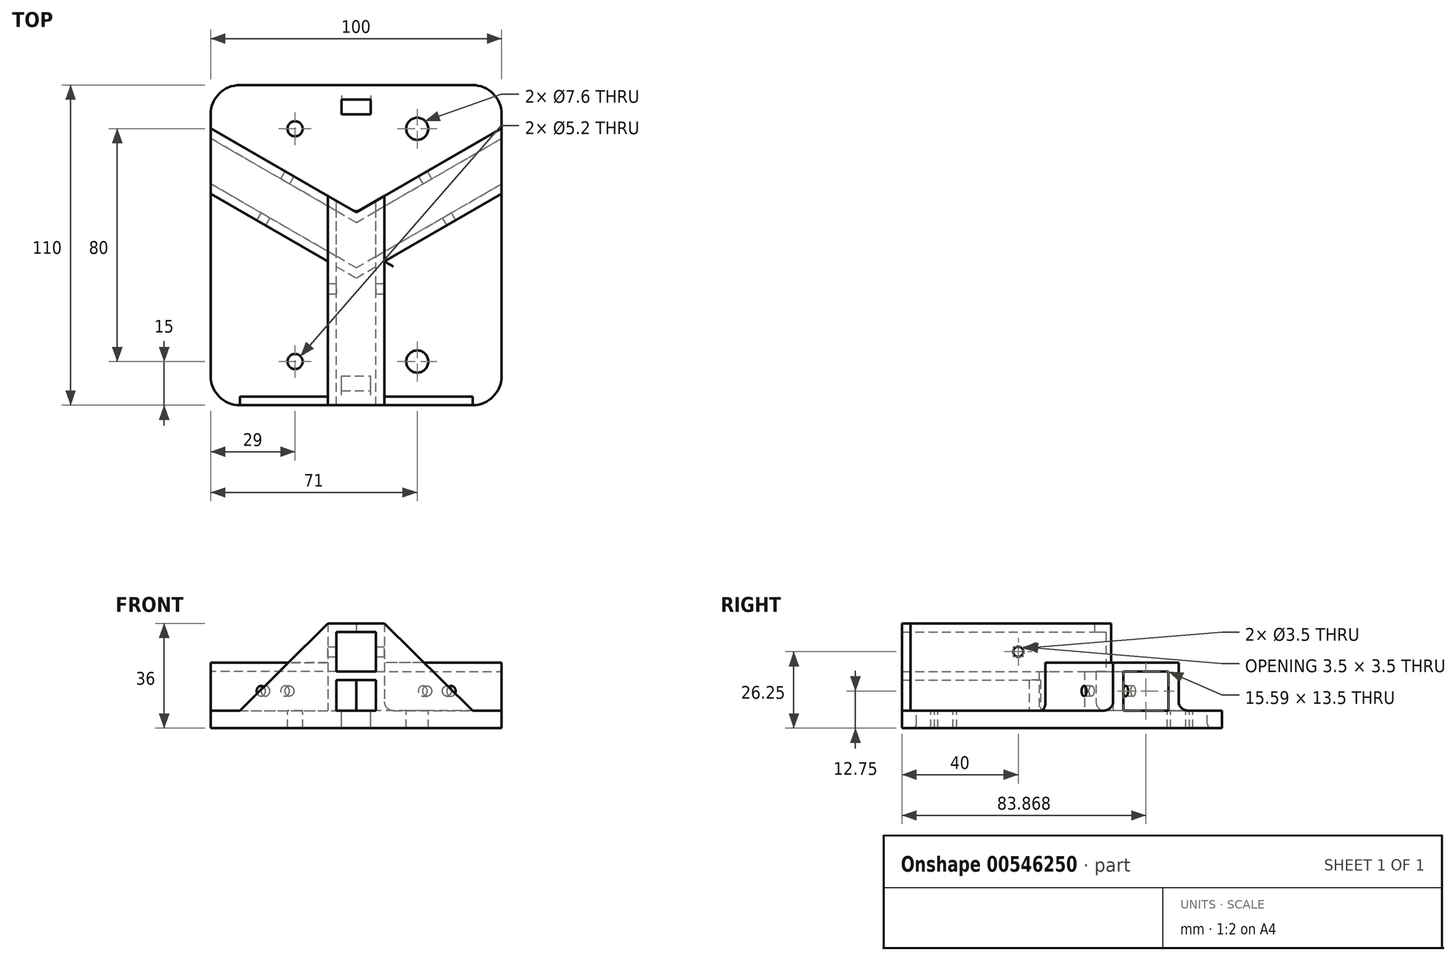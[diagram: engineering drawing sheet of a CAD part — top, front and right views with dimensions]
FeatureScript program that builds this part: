
annotation { "Feature Type Name" : "Feature", "Feature Type Description" : "" }
export const myFeature = defineFeature(function(context is Context, id is Id, definition is map)
    precondition{}
    {
        {
            var Q0;
            Q0=qCreatedBy(makeId("Top.planeOp"),FACE);
            var sketch = newSketch(context, id + "F0", { "sketchPlane" : qUnion([Q0])});
            skLineSegment(sketch, "E0.bottom", {"start": v(-50, 55) * mm, "end": v(50, 55) * mm});
            skLineSegment(sketch, "E0.top", {"start": v(-50, -55) * mm, "end": v(50, -55) * mm});
            skLineSegment(sketch, "E0.left", {"start": v(-50, 55) * mm, "end": v(-50, -55) * mm});
            skLineSegment(sketch, "E0.right", {"start": v(50, 55) * mm, "end": v(50, -55) * mm});
            skPoint(sketch, "E1", {"position": v(0, 55) * mm});
            skPoint(sketch, "E2", {"position": v(50, 0) * mm});
            skSolve(sketch);
        }
        {
            var Q0;
            Q0=qSketchRegion(id+"F0",true);
            extrude(context, id + "F1", {"entities" : qUnion([Q0]), "depth" : 6 * mm, "offsetDistance" : 25 * mm});
        }
        {
            var Q0;
            Q0=makeQuery(id+"F1.opExtrude","CAP_FACE",FACE,{"disambiguationData":[OSD([sQuery(id+"F0.wireOp",EDGE,"E0.bottom"),sQuery(id+"F0.wireOp",EDGE,"E0.top"),sQuery(id+"F0.wireOp",EDGE,"E0.left"),sQuery(id+"F0.wireOp",EDGE,"E0.right")])],"isStart":false});
            var sketch = newSketch(context, id + "F2", { "sketchPlane" : qUnion([Q0])});
            skLineSegment(sketch, "E3.bottom", {"start": v(-5, 50) * mm, "end": v(5, 50) * mm});
            skLineSegment(sketch, "E3.top", {"start": v(-5, 45) * mm, "end": v(5, 45) * mm});
            skLineSegment(sketch, "E3.left", {"start": v(-5, 50) * mm, "end": v(-5, 45) * mm});
            skLineSegment(sketch, "E3.right", {"start": v(5, 50) * mm, "end": v(5, 45) * mm});
            skPoint(sketch, "E4", {"position": v(0, 50) * mm});
            skLineSegment(sketch, "E5.MirrorCS", {"start": v(5, -50) * mm, "end": v(5, -45) * mm});
            skPoint(sketch, "E6.MirrorP", {"position": v(0, -50) * mm});
            skLineSegment(sketch, "E7.MirrorCS", {"start": v(-5, -50) * mm, "end": v(5, -50) * mm});
            skLineSegment(sketch, "E8.MirrorCS", {"start": v(-5, -50) * mm, "end": v(-5, -45) * mm});
            skLineSegment(sketch, "E9.MirrorCS", {"start": v(-5, -45) * mm, "end": v(5, -45) * mm});
            skSolve(sketch);
        }
        {
            var Q0;
            Q0=qSketchRegion(id+"F2",true);
            extrude(context, id + "F3", {"entities" : qUnion([Q0]), "operationType" : NewBodyOperationType.REMOVE, "endBound" : BoundingType.THROUGH_ALL, "oppositeDirection" : true, "depth" : 25 * mm, "offsetDistance" : 25 * mm});
        }
        {
            var Q0;
            Q0=makeQuery(id+"F1.opExtrude","CAP_FACE",FACE,{"disambiguationData":[OSD([sQuery(id+"F0.wireOp",EDGE,"E0.bottom"),sQuery(id+"F0.wireOp",EDGE,"E0.top"),sQuery(id+"F0.wireOp",EDGE,"E0.left"),sQuery(id+"F0.wireOp",EDGE,"E0.right")])],"isStart":false});
            var sketch = newSketch(context, id + "F4", { "sketchPlane" : qUnion([Q0])});
            skLineSegment(sketch, "E10", {"start": v(0, 0) * mm, "end": v(-68.17, 39.36) * mm, "construction": true});
            skLineSegment(sketch, "E11.MirrorCS", {"start": v(0, 0) * mm, "end": v(68.17, 39.36) * mm, "construction": true});
            skPoint(sketch, "E12.orphan", {"position": v(-19.52, -33.09) * mm});
            skPoint(sketch, "E13.right.end.orphan", {"position": v(19.52, -33.09) * mm});
            skLineSegment(sketch, "E14", {"start": v(0, -7.8) * mm, "end": v(50, 21.07) * mm});
            skLineSegment(sketch, "E15", {"start": v(50, 21.07) * mm, "end": v(50, 17.6) * mm});
            skLineSegment(sketch, "E16", {"start": v(50, 17.6) * mm, "end": v(9.75, -5.63) * mm});
            skLineSegment(sketch, "E17", {"start": v(0, 7.8) * mm, "end": v(50, 36.66) * mm});
            skLineSegment(sketch, "E18", {"start": v(50, 36.66) * mm, "end": v(50, 40.13) * mm});
            skLineSegment(sketch, "E19", {"start": v(50, 40.13) * mm, "end": v(0, 11.26) * mm});
            skLineSegment(sketch, "E20.MirrorCS", {"start": v(-50, 40.13) * mm, "end": v(0, 11.26) * mm});
            skLineSegment(sketch, "E21.MirrorCS", {"start": v(-50, 36.66) * mm, "end": v(-50, 40.13) * mm});
            skLineSegment(sketch, "E22.MirrorCS", {"start": v(0, 7.8) * mm, "end": v(-50, 36.66) * mm});
            skLineSegment(sketch, "E23.MirrorCS", {"start": v(0, -7.8) * mm, "end": v(-50, 21.07) * mm});
            skLineSegment(sketch, "E24.MirrorCS", {"start": v(-50, 21.07) * mm, "end": v(-50, 17.6) * mm});
            skLineSegment(sketch, "E25.MirrorCS", {"start": v(-50, 17.6) * mm, "end": v(-9.75, -5.63) * mm});
            skLineSegment(sketch, "E26", {"start": v(-6.75, -55) * mm, "end": v(-6.75, -7.36) * mm});
            skLineSegment(sketch, "E27", {"start": v(-9.75, -5.63) * mm, "end": v(-9.75, -55) * mm});
            skLineSegment(sketch, "E28", {"start": v(-9.75, -55) * mm, "end": v(-6.75, -55) * mm});
            skLineSegment(sketch, "E29.MirrorCS", {"start": v(9.75, -5.63) * mm, "end": v(9.75, -55) * mm});
            skLineSegment(sketch, "E30.MirrorCS", {"start": v(9.75, -55) * mm, "end": v(6.75, -55) * mm});
            skLineSegment(sketch, "E31.MirrorCS", {"start": v(6.75, -55) * mm, "end": v(6.75, -7.36) * mm});
            skLineSegment(sketch, "E32.trimOffspring", {"start": v(-6.75, -7.36) * mm, "end": v(0, -11.26) * mm});
            skLineSegment(sketch, "E33.trimOffspring", {"start": v(6.75, -7.36) * mm, "end": v(0, -11.26) * mm});
            skSolve(sketch);
        }
        {
            var Q0;
            {var subQ2=sQuery(id+"F0.wireOp",EDGE,"E0.right");var subQ3=makeQuery(id+"F1.opExtrude","SWEPT_FACE",FACE,{"disambiguationData":[OSD([subQ2])]});var subQ4=sQuery(id+"F0.wireOp",EDGE,"E0.top");var subQ5=makeQuery(id+"F1.opExtrude","SWEPT_FACE",FACE,{"disambiguationData":[OSD([subQ4])]});var subQ6=sQuery(id+"F0.wireOp",EDGE,"E0.left");Q0=makeQuery(id+"FRnbRCNZirlfwO5_1.boolean.opBoolean","SPLIT",FACE,{"disambiguationData":[TD([subQ3])],"derivedFrom":makeQuery(id+"F2k25GQCj0JztAD_1.boolean.opBoolean","SPLIT",FACE,{"disambiguationData":[TD([subQ5])],"derivedFrom":makeQuery(id+"F1.opExtrude","CAP_FACE",FACE,{"disambiguationData":[OSD([sQuery(id+"F0.wireOp",EDGE,"E0.bottom"),subQ4,subQ6,subQ2])],"isStart":false})})});}
            var sketch = newSketch(context, id + "F5", { "sketchPlane" : qUnion([Q0])});
            skCircle(sketch, "E34", {"center": v(21, -40) * mm, "radius": 3.8 * mm});
            skCircle(sketch, "E35", {"center": v(21, 40) * mm, "radius": 3.8 * mm});
            skCircle(sketch, "E36", {"center": v(-21, 40) * mm, "radius": 2.6 * mm});
            skCircle(sketch, "E37", {"center": v(-21, -40) * mm, "radius": 2.6 * mm});
            skSolve(sketch);
        }
        {
            var Q0;
            Q0=qSketchRegion(id+"F5",true);
            extrude(context, id + "F6", {"entities" : qUnion([Q0]), "operationType" : NewBodyOperationType.REMOVE, "endBound" : BoundingType.THROUGH_ALL, "oppositeDirection" : true, "depth" : 25 * mm, "offsetDistance" : 25 * mm});
        }
        {
            var Q0;
            Q0=qSketchRegion(id+"F4",true);
            extrude(context, id + "F7", {"entities" : qUnion([Q0]), "operationType" : NewBodyOperationType.ADD, "depth" : 13.5 * mm, "offsetDistance" : 25 * mm});
        }
        {
            var Q0;
            {var subQ0=sQuery(id+"F0.wireOp",EDGE,"E0.top");Q0=makeQuery(id+"F7.boolean.opBoolean","SPLIT",FACE,{"disambiguationData":[TD([makeQuery(id+"F3.boolean.opBoolean","COPY",FACE,{"derivedFrom":makeQuery(id+"F3.opExtrude","SWEPT_FACE",FACE,{"disambiguationData":[OSD([sQuery(id+"F2.wireOp",EDGE,"E5.MirrorCS")])]})})])],"derivedFrom":makeQuery(id+"F1.opExtrude","CAP_FACE",FACE,{"disambiguationData":[OSD([sQuery(id+"F0.wireOp",EDGE,"E0.bottom"),subQ0,sQuery(id+"F0.wireOp",EDGE,"E0.left"),sQuery(id+"F0.wireOp",EDGE,"E0.right")])],"isStart":false})});}
            cPlane(context, id + "F8", {"entities" : qUnion([Q0]), "cplaneType" : CPlaneType.OFFSET, "offset" : 13.5 * mm, "width" : 150 * mm, "height" : 150 * mm});
        }
        {
            var Q0;
            Q0=makeQuery(id+"F7.opExtrude","CAP_FACE",FACE,{"disambiguationData":[OSD([sQuery(id+"F4.wireOp",EDGE,"E14"),sQuery(id+"F4.wireOp",EDGE,"E15"),sQuery(id+"F4.wireOp",EDGE,"E16"),sQuery(id+"F4.wireOp",EDGE,"E23.MirrorCS"),sQuery(id+"F4.wireOp",EDGE,"E24.MirrorCS"),sQuery(id+"F4.wireOp",EDGE,"E25.MirrorCS"),sQuery(id+"F4.wireOp",EDGE,"E26"),sQuery(id+"F4.wireOp",EDGE,"E27"),sQuery(id+"F4.wireOp",EDGE,"E28"),sQuery(id+"F4.wireOp",EDGE,"E29.MirrorCS"),sQuery(id+"F4.wireOp",EDGE,"E30.MirrorCS"),sQuery(id+"F4.wireOp",EDGE,"E31.MirrorCS"),sQuery(id+"F4.wireOp",EDGE,"E32.trimOffspring"),sQuery(id+"F4.wireOp",EDGE,"E33.trimOffspring")])],"isStart":false});
            var sketch = newSketch(context, id + "F9", { "sketchPlane" : qUnion([Q0])});
            skLineSegment(sketch, "E38", {"start": v(-9.75, -55) * mm, "end": v(-9.75, 16.89) * mm});
            skLineSegment(sketch, "E39", {"start": v(-9.75, -55) * mm, "end": v(-6.75, -55) * mm});
            skLineSegment(sketch, "E40", {"start": v(-6.75, -55) * mm, "end": v(-6.75, 15.16) * mm});
            skLineSegment(sketch, "E41", {"start": v(-6.75, 15.16) * mm, "end": v(-9.75, 16.89) * mm});
            skLineSegment(sketch, "E42.MirrorCS", {"start": v(6.75, 15.16) * mm, "end": v(9.75, 16.89) * mm});
            skLineSegment(sketch, "E43.MirrorCS", {"start": v(9.75, -55) * mm, "end": v(6.75, -55) * mm});
            skLineSegment(sketch, "E44.MirrorCS", {"start": v(9.75, -55) * mm, "end": v(9.75, 16.89) * mm});
            skLineSegment(sketch, "E45.MirrorCS", {"start": v(6.75, -55) * mm, "end": v(6.75, 15.16) * mm});
            skSolve(sketch);
        }
        {
            var Q0;
            Q0=qSketchRegion(id+"F9",true);
            extrude(context, id + "F10", {"entities" : qUnion([Q0]), "operationType" : NewBodyOperationType.ADD, "depth" : 13.5 * mm, "offsetDistance" : 25 * mm});
        }
        {
            var Q0;
            {var subQ0=sQuery(id+"F4.wireOp",EDGE,"E15");var subQ1=sQuery(id+"F4.wireOp",EDGE,"E14");var subQ2=sQuery(id+"F4.wireOp",EDGE,"E16");var subQ4=sQuery(id+"F4.wireOp",EDGE,"E29.MirrorCS");Q0=makeQuery(id+"F10.boolean.opBoolean","SPLIT",FACE,{"disambiguationData":[TD([makeQuery(id+"F1.opExtrude","SWEPT_FACE",FACE,{"disambiguationData":[OSD([sQuery(id+"F0.wireOp",EDGE,"E0.right")])]})])],"derivedFrom":makeQuery(id+"F7.opExtrude","CAP_FACE",FACE,{"disambiguationData":[OSD([subQ1,subQ0,subQ2,sQuery(id+"F4.wireOp",EDGE,"E23.MirrorCS"),sQuery(id+"F4.wireOp",EDGE,"E24.MirrorCS"),sQuery(id+"F4.wireOp",EDGE,"E25.MirrorCS"),sQuery(id+"F4.wireOp",EDGE,"E26"),sQuery(id+"F4.wireOp",EDGE,"E27"),sQuery(id+"F4.wireOp",EDGE,"E28"),subQ4,sQuery(id+"F4.wireOp",EDGE,"E30.MirrorCS"),sQuery(id+"F4.wireOp",EDGE,"E31.MirrorCS"),sQuery(id+"F4.wireOp",EDGE,"E32.trimOffspring"),sQuery(id+"F4.wireOp",EDGE,"E33.trimOffspring")])],"isStart":false})});}
            var sketch = newSketch(context, id + "F11", { "sketchPlane" : qUnion([Q0])});
            skLineSegment(sketch, "E46", {"start": v(9.75, -5.63) * mm, "end": v(50, 17.6) * mm});
            skLineSegment(sketch, "E47", {"start": v(50, 17.6) * mm, "end": v(50, 40.13) * mm});
            skLineSegment(sketch, "E48", {"start": v(50, 40.13) * mm, "end": v(9.75, 16.89) * mm});
            skLineSegment(sketch, "E49", {"start": v(9.75, 16.89) * mm, "end": v(9.75, -5.63) * mm});
            skLineSegment(sketch, "E50.MirrorCS", {"start": v(-50, 17.6) * mm, "end": v(-50, 40.13) * mm});
            skLineSegment(sketch, "E51.MirrorCS", {"start": v(-9.75, -5.63) * mm, "end": v(-50, 17.6) * mm});
            skLineSegment(sketch, "E52.MirrorCS", {"start": v(-50, 40.13) * mm, "end": v(-9.75, 16.89) * mm});
            skLineSegment(sketch, "E53.MirrorCS", {"start": v(-9.75, 16.89) * mm, "end": v(-9.75, -5.63) * mm});
            skSolve(sketch);
        }
        {
            var Q0;
            Q0=qSketchRegion(id+"F11",true);
            extrude(context, id + "F12", {"entities" : qUnion([Q0]), "operationType" : NewBodyOperationType.ADD, "depth" : 3 * mm, "offsetDistance" : 25 * mm});
        }
        {
            var Q0;
            Q0=qCreatedBy(id+"F8.planeOp",FACE);
            var sketch = newSketch(context, id + "F13", { "sketchPlane" : qUnion([Q0])});
            skLineSegment(sketch, "E54", {"start": v(-6.75, -55) * mm, "end": v(-6.75, -7.36) * mm});
            skLineSegment(sketch, "E55", {"start": v(-6.75, -7.36) * mm, "end": v(0, -11.26) * mm});
            skLineSegment(sketch, "E56", {"start": v(0, -11.26) * mm, "end": v(6.75, -7.36) * mm});
            skLineSegment(sketch, "E57", {"start": v(6.75, -7.36) * mm, "end": v(6.75, -55) * mm});
            skLineSegment(sketch, "E58", {"start": v(6.75, -55) * mm, "end": v(-6.75, -55) * mm});
            skSolve(sketch);
        }
        {
            var Q0;
            Q0 = qSketchRegion(id + "F13", true);
            extrude(context, id + "F14", {"entities" : qUnion([Q0]), "operationType" : NewBodyOperationType.ADD, "oppositeDirection" : true, "depth" : 3 * mm, "offsetDistance" : 25 * mm});
        }
        {
            var Q0;
            Q0=makeQuery(id+"F10.opExtrude","CAP_FACE",FACE,{"disambiguationData":[OSD([sQuery(id+"F9.wireOp",EDGE,"E38"),sQuery(id+"F9.wireOp",EDGE,"E39"),sQuery(id+"F9.wireOp",EDGE,"E40"),sQuery(id+"F9.wireOp",EDGE,"E41")])],"isStart":false});
            var sketch = newSketch(context, id + "F15", { "sketchPlane" : qUnion([Q0])});
            skLineSegment(sketch, "E59", {"start": v(-9.75, 16.89) * mm, "end": v(-9.75, -55) * mm});
            skLineSegment(sketch, "E60", {"start": v(-9.75, -55) * mm, "end": v(9.75, -55) * mm});
            skLineSegment(sketch, "E61", {"start": v(-9.75, 16.89) * mm, "end": v(0, 11.26) * mm});
            skLineSegment(sketch, "E62", {"start": v(0, 11.26) * mm, "end": v(9.75, 16.89) * mm});
            skLineSegment(sketch, "E63", {"start": v(9.75, 16.89) * mm, "end": v(9.75, -55) * mm});
            skSolve(sketch);
        }
        {
            var Q0;
            Q0 = qSketchRegion(id + "F15", true);
            extrude(context, id + "F16", {"entities" : qUnion([Q0]), "operationType" : NewBodyOperationType.ADD, "depth" : 3 * mm, "offsetDistance" : 25 * mm});
        }
        {
            var Q0;
            Q0=makeQuery(id+"F12.boolean.opBoolean","MERGE",FACE,{"derivedFrom":[makeQuery(id+"F7.opExtrude","SWEPT_FACE",FACE,{"disambiguationData":[OSD([sQuery(id+"F4.wireOp",EDGE,"E16")])]}),makeQuery(id+"F12.opExtrude","SWEPT_FACE",FACE,{"disambiguationData":[OSD([sQuery(id+"F11.wireOp",EDGE,"E46")])]})]});
            var sketch = newSketch(context, id + "F17", { "sketchPlane" : qUnion([Q0])});
            skCircle(sketch, "E64", {"center": v(32.1, 12.75) * mm, "radius": 1.75 * mm});
            skSolve(sketch);
        }
        {
            var Q0;
            Q0=qSketchRegion(id+"F17",true);
            extrude(context, id + "F18", {"entities" : qUnion([Q0]), "operationType" : NewBodyOperationType.REMOVE, "endBound" : BoundingType.THROUGH_ALL, "oppositeDirection" : true, "depth" : 25 * mm, "offsetDistance" : 25 * mm});
        }
        {
            var Q0;
            Q0=makeQuery(id+"F12.boolean.opBoolean","MERGE",FACE,{"derivedFrom":[makeQuery(id+"F7.opExtrude","SWEPT_FACE",FACE,{"disambiguationData":[OSD([sQuery(id+"F4.wireOp",EDGE,"E25.MirrorCS")])]}),makeQuery(id+"F12.opExtrude","SWEPT_FACE",FACE,{"disambiguationData":[OSD([sQuery(id+"F11.wireOp",EDGE,"E51.MirrorCS")])]})]});
            var sketch = newSketch(context, id + "F19", { "sketchPlane" : qUnion([Q0])});
            skCircle(sketch, "E65", {"center": v(-32.1, 12.75) * mm, "radius": 1.75 * mm});
            skSolve(sketch);
        }
        {
            var Q0;
            Q0=qSketchRegion(id+"F19",true);
            extrude(context, id + "F20", {"entities" : qUnion([Q0]), "operationType" : NewBodyOperationType.REMOVE, "endBound" : BoundingType.THROUGH_ALL, "oppositeDirection" : true, "depth" : 25 * mm, "offsetDistance" : 25 * mm});
        }
        {
            var Q0;
            Q0=makeQuery(id+"F3.boolean.opBoolean","COPY",EDGE,{"derivedFrom":makeQuery(id+"F3.opExtrude","CAP_EDGE",EDGE,{"disambiguationData":[OSD([sQuery(id+"F2.wireOp",EDGE,"E3.bottom")])],"isStart":true})});
            var Q1;
            Q1=makeQuery(id+"F3.boolean.opBoolean","INTERSECT",EDGE,{"derivedFrom":[makeQuery(id+"F1.opExtrude","CAP_FACE",FACE,{"disambiguationData":[OSD([sQuery(id+"F0.wireOp",EDGE,"E0.bottom"),sQuery(id+"F0.wireOp",EDGE,"E0.top"),sQuery(id+"F0.wireOp",EDGE,"E0.left"),sQuery(id+"F0.wireOp",EDGE,"E0.right")])],"isStart":true}),makeQuery(id+"F3.opExtrude","SWEPT_FACE",FACE,{"disambiguationData":[OSD([sQuery(id+"F2.wireOp",EDGE,"E3.bottom")])]})]});
            var Q2;
            Q2=makeQuery(id+"F3.boolean.opBoolean","INTERSECT",EDGE,{"derivedFrom":[makeQuery(id+"F1.opExtrude","CAP_FACE",FACE,{"disambiguationData":[OSD([sQuery(id+"F0.wireOp",EDGE,"E0.bottom"),sQuery(id+"F0.wireOp",EDGE,"E0.top"),sQuery(id+"F0.wireOp",EDGE,"E0.left"),sQuery(id+"F0.wireOp",EDGE,"E0.right")])],"isStart":true}),makeQuery(id+"F3.opExtrude","SWEPT_FACE",FACE,{"disambiguationData":[OSD([sQuery(id+"F2.wireOp",EDGE,"E7.MirrorCS")])]})]});
            var Q3;
            Q3=makeQuery(id+"F3.boolean.opBoolean","COPY",EDGE,{"derivedFrom":makeQuery(id+"F3.opExtrude","CAP_EDGE",EDGE,{"disambiguationData":[OSD([sQuery(id+"F2.wireOp",EDGE,"E7.MirrorCS")])],"isStart":true})});
            fillet(context, id + "F21", {"entities" : qUnion([Q0, Q1, Q2, Q3]), "radius" : 1.5 * mm, "tangentPropagation" : true, "allowEdgeOverflow" : false});
        }
        {
            var Q0;
            Q0=makeQuery(id+"F1.opExtrude","SWEPT_EDGE",EDGE,{"disambiguationData":[OSD([sQuery(id+"F0.wireOp",EDGE,"E0.top"),sQuery(id+"F0.wireOp",EDGE,"E0.left")])]});
            var Q1;
            Q1=makeQuery(id+"F1.opExtrude","SWEPT_EDGE",EDGE,{"disambiguationData":[OSD([sQuery(id+"F0.wireOp",EDGE,"E0.top"),sQuery(id+"F0.wireOp",EDGE,"E0.right")])]});
            var Q2;
            Q2=makeQuery(id+"F1.opExtrude","SWEPT_EDGE",EDGE,{"disambiguationData":[OSD([sQuery(id+"F0.wireOp",EDGE,"E0.bottom"),sQuery(id+"F0.wireOp",EDGE,"E0.right")])]});
            var Q3;
            Q3=makeQuery(id+"F1.opExtrude","SWEPT_EDGE",EDGE,{"disambiguationData":[OSD([sQuery(id+"F0.wireOp",EDGE,"E0.bottom"),sQuery(id+"F0.wireOp",EDGE,"E0.left")])]});
            fillet(context, id + "F22", {"entities" : qUnion([Q0, Q1, Q2, Q3]), "radius" : 10 * mm, "tangentPropagation" : true, "allowEdgeOverflow" : false});
        }
        {
            var Q0;
            Q0=makeQuery(id+"F16.boolean.opBoolean","MERGE",FACE,{"derivedFrom":[makeQuery(id+"F14.boolean.opBoolean","MERGE",FACE,{"derivedFrom":[makeQuery(id+"F10.boolean.opBoolean","MERGE",FACE,{"derivedFrom":[makeQuery(id+"F7.boolean.opBoolean","MERGE",FACE,{"derivedFrom":[makeQuery(id+"F1.opExtrude","SWEPT_FACE",FACE,{"disambiguationData":[OSD([sQuery(id+"F0.wireOp",EDGE,"E0.top")])]}),makeQuery(id+"F7.opExtrude","SWEPT_FACE",FACE,{"disambiguationData":[OSD([sQuery(id+"F4.wireOp",EDGE,"E28")])]}),makeQuery(id+"F7.opExtrude","SWEPT_FACE",FACE,{"disambiguationData":[OSD([sQuery(id+"F4.wireOp",EDGE,"E30.MirrorCS")])]})]}),makeQuery(id+"F10.opExtrude","SWEPT_FACE",FACE,{"disambiguationData":[OSD([sQuery(id+"F9.wireOp",EDGE,"E39")])]}),makeQuery(id+"F10.opExtrude","SWEPT_FACE",FACE,{"disambiguationData":[OSD([sQuery(id+"F9.wireOp",EDGE,"E43.MirrorCS")])]})]}),makeQuery(id+"F14.opExtrude","SWEPT_FACE",FACE,{"disambiguationData":[OSD([sQuery(id+"F13.wireOp",EDGE,"E58")])]})]}),makeQuery(id+"F16.opExtrude","SWEPT_FACE",FACE,{"disambiguationData":[OSD([sQuery(id+"F15.wireOp",EDGE,"E60")])]})]});
            var sketch = newSketch(context, id + "F23", { "sketchPlane" : qUnion([Q0])});
            skLineSegment(sketch, "E66", {"start": v(-9.75, 36) * mm, "end": v(-40, 6) * mm});
            skLineSegment(sketch, "E67", {"start": v(-40, 6) * mm, "end": v(-9.75, 6) * mm});
            skLineSegment(sketch, "E68", {"start": v(-9.75, 6) * mm, "end": v(-9.75, 36) * mm});
            skLineSegment(sketch, "E69.MirrorCS", {"start": v(40, 6) * mm, "end": v(9.75, 6) * mm});
            skLineSegment(sketch, "E70.MirrorCS", {"start": v(9.75, 36) * mm, "end": v(40, 6) * mm});
            skLineSegment(sketch, "E71.MirrorCS", {"start": v(9.75, 6) * mm, "end": v(9.75, 36) * mm});
            skSolve(sketch);
        }
        {
            var Q0;
            Q0 = qSketchRegion(id + "F23", true);
            extrude(context, id + "F24", {"entities" : qUnion([Q0]), "operationType" : NewBodyOperationType.ADD, "oppositeDirection" : true, "depth" : 3 * mm, "offsetDistance" : 25 * mm});
        }
        {
            var Q0;
            Q0=makeQuery(id+"F12.opExtrude","CAP_EDGE",EDGE,{"disambiguationData":[OSD([sQuery(id+"F11.wireOp",EDGE,"E53.MirrorCS")])],"isStart":false});
            var Q1;
            Q1=makeQuery(id+"F7.opExtrude","CAP_EDGE",EDGE,{"disambiguationData":[OSD([sQuery(id+"F4.wireOp",EDGE,"E27")])],"isStart":true});
            var Q2;
            Q2=makeQuery(id+"F12.boolean.opBoolean","MERGE",EDGE,{"derivedFrom":[makeQuery(id+"F7.opExtrude","SWEPT_EDGE",EDGE,{"disambiguationData":[OSD([sQuery(id+"F4.wireOp",EDGE,"E25.MirrorCS"),sQuery(id+"F4.wireOp",EDGE,"E27")])]}),makeQuery(id+"F12.opExtrude","SWEPT_EDGE",EDGE,{"disambiguationData":[OSD([sQuery(id+"F11.wireOp",EDGE,"E51.MirrorCS"),sQuery(id+"F11.wireOp",EDGE,"E53.MirrorCS")])]})]});
            var Q3;
            Q3=makeQuery(id+"F7.opExtrude","CAP_EDGE",EDGE,{"disambiguationData":[OSD([sQuery(id+"F4.wireOp",EDGE,"E25.MirrorCS")])],"isStart":true});
            var Q4;
            Q4=makeQuery(id+"F7.opExtrude","CAP_EDGE",EDGE,{"disambiguationData":[OSD([sQuery(id+"F4.wireOp",EDGE,"E29.MirrorCS")])],"isStart":true});
            var Q5;
            Q5=makeQuery(id+"F12.boolean.opBoolean","MERGE",EDGE,{"derivedFrom":[makeQuery(id+"F7.opExtrude","SWEPT_EDGE",EDGE,{"disambiguationData":[OSD([sQuery(id+"F4.wireOp",EDGE,"E16"),sQuery(id+"F4.wireOp",EDGE,"E29.MirrorCS")])]}),makeQuery(id+"F12.opExtrude","SWEPT_EDGE",EDGE,{"disambiguationData":[OSD([sQuery(id+"F11.wireOp",EDGE,"E46"),sQuery(id+"F11.wireOp",EDGE,"E49")])]})]});
            var Q6;
            Q6=makeQuery(id+"F12.opExtrude","CAP_EDGE",EDGE,{"disambiguationData":[OSD([sQuery(id+"F11.wireOp",EDGE,"E49")])],"isStart":false});
            var Q7;
            Q7=makeQuery(id+"F7.opExtrude","CAP_EDGE",EDGE,{"disambiguationData":[OSD([sQuery(id+"F4.wireOp",EDGE,"E16")])],"isStart":true});
            var Q8;
            Q8=makeQuery(id+"F24.opExtrude","CAP_EDGE",EDGE,{"disambiguationData":[OSD([sQuery(id+"F23.wireOp",EDGE,"E69.MirrorCS")])],"isStart":false});
            var Q9;
            Q9=makeQuery(id+"F24.opExtrude","CAP_EDGE",EDGE,{"disambiguationData":[OSD([sQuery(id+"F23.wireOp",EDGE,"E67")])],"isStart":false});
            var Q10;
            Q10=makeQuery(id+"F7.opExtrude","CAP_EDGE",EDGE,{"disambiguationData":[OSD([sQuery(id+"F4.wireOp",EDGE,"E19")])],"isStart":true});
            var Q11;
            Q11=makeQuery(id+"F7.opExtrude","CAP_EDGE",EDGE,{"disambiguationData":[OSD([sQuery(id+"F4.wireOp",EDGE,"E20.MirrorCS")])],"isStart":true});
            var Q12;
            Q12=makeQuery(id+"F7.opExtrude","SWEPT_EDGE",EDGE,{"disambiguationData":[OSD([sQuery(id+"F4.wireOp",EDGE,"E19"),sQuery(id+"F4.wireOp",EDGE,"E20.MirrorCS")])]});
            var Q13;
            Q13=makeQuery(id+"F24.opExtrude","CAP_EDGE",EDGE,{"disambiguationData":[OSD([sQuery(id+"F23.wireOp",EDGE,"E71.MirrorCS")])],"isStart":false});
            var Q14;
            Q14=makeQuery(id+"F24.opExtrude","CAP_EDGE",EDGE,{"disambiguationData":[OSD([sQuery(id+"F23.wireOp",EDGE,"E68")])],"isStart":false});
            fillet(context, id + "F25", {"entities" : qUnion([Q0, Q1, Q2, Q3, Q4, Q5, Q6, Q7, Q8, Q9, Q10, Q11, Q12, Q13, Q14]), "radius" : 3 * mm, "tangentPropagation" : true, "allowEdgeOverflow" : false});
        }
        {
            var Q0;
            Q0=makeQuery(id+"F16.boolean.opBoolean","MERGE",FACE,{"derivedFrom":[makeQuery(id+"F10.boolean.opBoolean","MERGE",FACE,{"derivedFrom":[makeQuery(id+"F7.opExtrude","SWEPT_FACE",FACE,{"disambiguationData":[OSD([sQuery(id+"F4.wireOp",EDGE,"E29.MirrorCS")])]}),makeQuery(id+"F10.opExtrude","SWEPT_FACE",FACE,{"disambiguationData":[OSD([sQuery(id+"F9.wireOp",EDGE,"E44.MirrorCS")])]})]}),makeQuery(id+"F16.opExtrude","SWEPT_FACE",FACE,{"disambiguationData":[OSD([sQuery(id+"F15.wireOp",EDGE,"E63")])]})]});
            var sketch = newSketch(context, id + "F26", { "sketchPlane" : qUnion([Q0])});
            skCircle(sketch, "E72", {"center": v(-15, 26.25) * mm, "radius": 1.75 * mm});
            skSolve(sketch);
        }
        {
            var Q0;
            Q0 = qSketchRegion(id + "F26", true);
            extrude(context, id + "F27", {"entities" : qUnion([Q0]), "operationType" : NewBodyOperationType.REMOVE, "endBound" : BoundingType.THROUGH_ALL, "oppositeDirection" : true, "depth" : 25 * mm, "offsetDistance" : 25 * mm});
        }
    });
